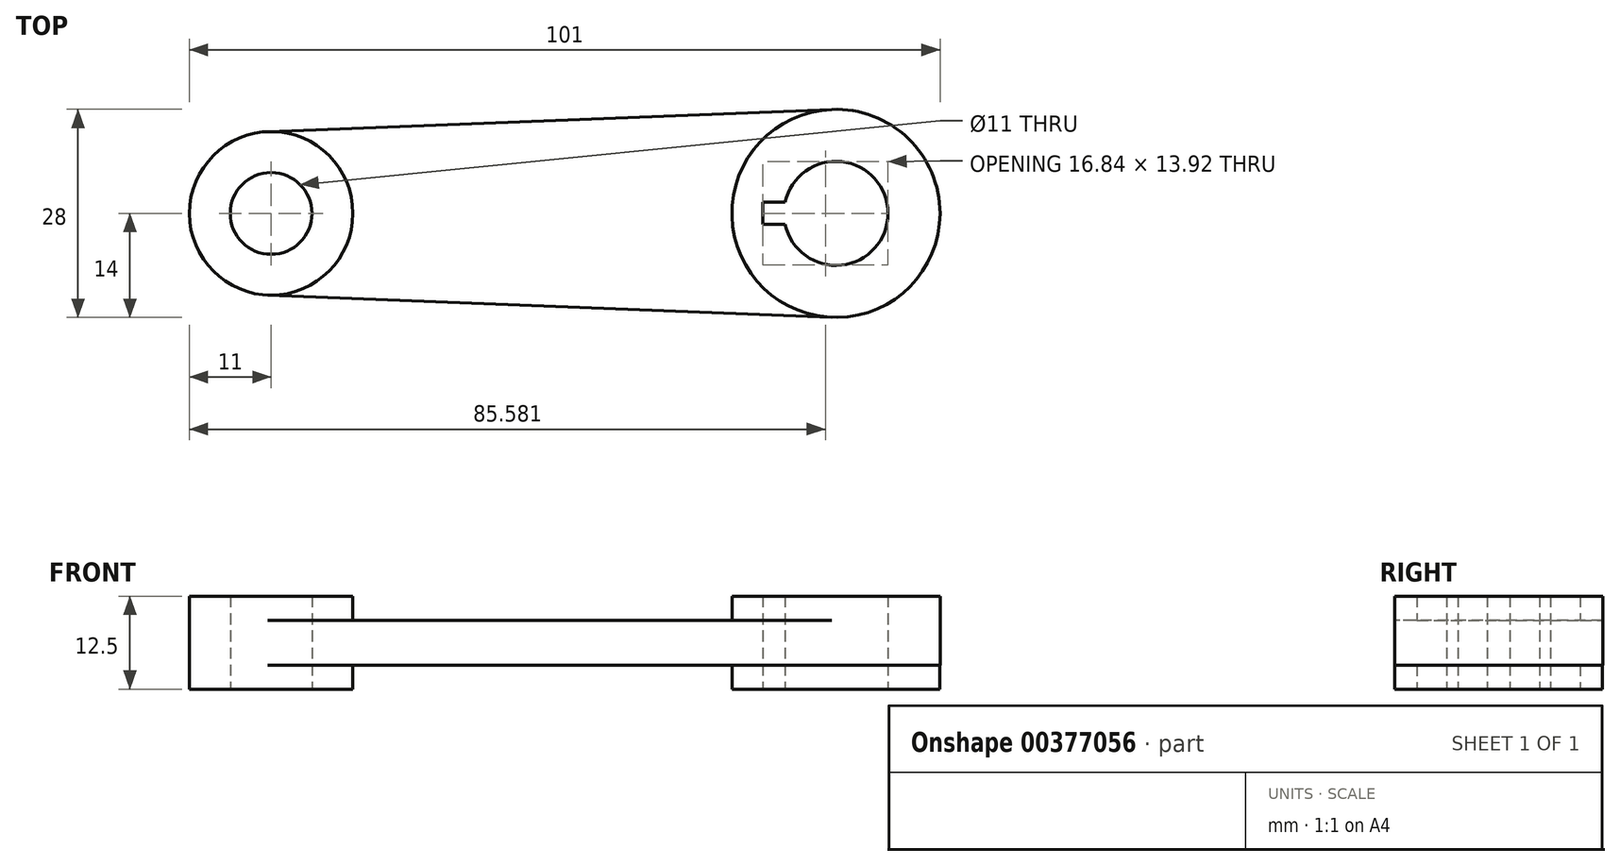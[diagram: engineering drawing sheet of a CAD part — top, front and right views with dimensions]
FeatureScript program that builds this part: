
annotation { "Feature Type Name" : "Feature", "Feature Type Description" : "" }
export const myFeature = defineFeature(function(context is Context, id is Id, definition is map)
    precondition{}
    {
        {
            var Q0;
            Q0=qCreatedBy(makeId("Top.planeOp"),FACE);
            var sketch = newSketch(context, id + "F0", { "sketchPlane" : qUnion([Q0])});
            skPoint(sketch, "E0", {"position": v(0, 0) * mm});
            skPoint(sketch, "E1", {"position": v(-38, 0) * mm});
            skPoint(sketch, "E2", {"position": v(38, 0) * mm});
            skArc(sketch, "E3", {"start": v(31.16, -1.5) * mm, "mid": v(45, 0) * mm, "end": v(31.16, 1.5) * mm});
            skCircle(sketch, "E4", {"center": v(38, 0) * mm, "radius": 14 * mm});
            skCircle(sketch, "E5", {"center": v(-38, 0) * mm, "radius": 5.5 * mm});
            skCircle(sketch, "E6", {"center": v(-38, 0) * mm, "radius": 11 * mm});
            skLineSegment(sketch, "E7", {"start": v(-38.43, 11) * mm, "end": v(37.45, 13.99) * mm});
            skLineSegment(sketch, "E8.MirrorCS", {"start": v(-38.43, -11) * mm, "end": v(37.45, -13.99) * mm});
            skLineSegment(sketch, "E9", {"start": v(28.16, 1.5) * mm, "end": v(31.16, 1.5) * mm});
            skLineSegment(sketch, "E10", {"start": v(28.16, -1.5) * mm, "end": v(31.16, -1.5) * mm});
            skLineSegment(sketch, "E11", {"start": v(28.16, 1.5) * mm, "end": v(28.16, -1.5) * mm});
            skPoint(sketch, "E12", {"position": v(28.16, 13.62) * mm});
            skPoint(sketch, "E13", {"position": v(28.16, -13.62) * mm});
            skArc(sketch, "E14", {"start": v(27.81, 13.6) * mm, "mid": v(21, 0) * mm, "end": v(27.81, -13.6) * mm});
            skPoint(sketch, "E15", {"position": v(21, 0) * mm});
            skPoint(sketch, "E16", {"position": v(24, 0) * mm});
            skPoint(sketch, "E17", {"position": v(-27, 0) * mm});
            skPoint(sketch, "E18", {"position": v(-24, 0) * mm});
            skArc(sketch, "E19", {"start": v(-29.78, -11.33) * mm, "mid": v(-24, 0) * mm, "end": v(-29.78, 11.33) * mm});
            skSolve(sketch);
        }
        {
            var Q0;
            {var subQ0=sQuery(id+"F0.wireOp",EDGE,"E14");Q0=makeQuery(id+"F0.imprint","IMPRINT",FACE,{"disambiguationData":[TD([[makeQuery(id+"F0.imprint","IMPRINT",EDGE,{"derivedFrom":subQ0}),-1.0]])]});}
            var Q1;
            {var subQ5=sQuery(id+"F0.wireOp",EDGE,"E19");Q1=makeQuery(id+"F0.imprint","IMPRINT",FACE,{"disambiguationData":[TD([[makeQuery(id+"F0.imprint","IMPRINT",EDGE,{"derivedFrom":subQ5}),1.0]])]});}
            var Q2;
            Q2=makeQuery(id+"F0.imprint","IMPRINT",FACE,{"disambiguationData":[TD([[makeQuery(id+"F0.imprint","IMPRINT",EDGE,{"derivedFrom":sQuery(id+"F0.wireOp",EDGE,"E5")}),-1.0]])]});
            var Q3;
            {var subQ5=sQuery(id+"F0.wireOp",EDGE,"E14");Q3=makeQuery(id+"F0.imprint","IMPRINT",FACE,{"disambiguationData":[TD([[makeQuery(id+"F0.imprint","IMPRINT",EDGE,{"derivedFrom":subQ5}),1.0]])]});}
            var Q4;
            Q4=makeQuery(id+"F0.imprint","IMPRINT",FACE,{"disambiguationData":[TD([[makeQuery(id+"F0.imprint","IMPRINT",EDGE,{"derivedFrom":sQuery(id+"F0.wireOp",EDGE,"E3")}),-1.0]])]});
            extrude(context, id + "F1", {"entities" : qUnion([Q0, Q1, Q2, Q3, Q4]), "depth" : 6 * mm});
        }
        {
            var Q0;
            Q0=makeQuery(id+"F1.opExtrude","CAP_FACE",FACE,{"disambiguationData":[OSD([sQuery(id+"F0.wireOp",EDGE,"E3"),sQuery(id+"F0.wireOp",EDGE,"E4"),sQuery(id+"F0.wireOp",EDGE,"E5"),sQuery(id+"F0.wireOp",EDGE,"E6"),sQuery(id+"F0.wireOp",EDGE,"E7"),sQuery(id+"F0.wireOp",EDGE,"E8.MirrorCS"),sQuery(id+"F0.wireOp",EDGE,"E9"),sQuery(id+"F0.wireOp",EDGE,"E10"),sQuery(id+"F0.wireOp",EDGE,"E11")])],"isStart":true});
            var sketch = newSketch(context, id + "F2", { "sketchPlane" : qUnion([Q0])});
            skPoint(sketch, "E20.0", {"position": v(0, 0) * mm});
            skPoint(sketch, "E20.1", {"position": v(-38, 0) * mm});
            skPoint(sketch, "E20.2", {"position": v(38, 0) * mm});
            skArc(sketch, "E20.3", {"start": v(31.16, 1.5) * mm, "mid": v(45, 0) * mm, "end": v(31.16, -1.5) * mm});
            skCircle(sketch, "E20.4", {"center": v(38, 0) * mm, "radius": 14 * mm});
            skCircle(sketch, "E20.5", {"center": v(-38, 0) * mm, "radius": 5.5 * mm});
            skCircle(sketch, "E20.6", {"center": v(-38, 0) * mm, "radius": 11 * mm});
            skLineSegment(sketch, "E20.7", {"start": v(-38.43, -11) * mm, "end": v(37.45, -13.99) * mm});
            skLineSegment(sketch, "E20.8", {"start": v(-38.43, 11) * mm, "end": v(37.45, 13.99) * mm});
            skLineSegment(sketch, "E20.9", {"start": v(28.16, -1.5) * mm, "end": v(31.16, -1.5) * mm});
            skLineSegment(sketch, "E20.10", {"start": v(28.16, 1.5) * mm, "end": v(31.16, 1.5) * mm});
            skLineSegment(sketch, "E20.11", {"start": v(28.16, -1.5) * mm, "end": v(28.16, 1.5) * mm});
            skPoint(sketch, "E20.12", {"position": v(28.16, -13.62) * mm});
            skPoint(sketch, "E20.13", {"position": v(28.16, 13.62) * mm});
            skArc(sketch, "E20.14", {"start": v(27.81, -13.6) * mm, "mid": v(21, 0) * mm, "end": v(27.81, 13.6) * mm});
            skPoint(sketch, "E20.15", {"position": v(21, 0) * mm});
            skPoint(sketch, "E20.16", {"position": v(24, 0) * mm});
            skPoint(sketch, "E20.17", {"position": v(-27, 0) * mm});
            skPoint(sketch, "E20.18", {"position": v(-24, 0) * mm});
            skArc(sketch, "E20.19", {"start": v(-29.78, 11.33) * mm, "mid": v(-24, 0) * mm, "end": v(-29.78, -11.33) * mm});
            skPoint(sketch, "E21", {"position": v(37.45, -13.99) * mm});
            skPoint(sketch, "E22", {"position": v(37.45, 13.99) * mm});
            skPoint(sketch, "E23", {"position": v(31.16, -1.5) * mm});
            skPoint(sketch, "E24", {"position": v(28.16, -1.5) * mm});
            skPoint(sketch, "E25", {"position": v(28.16, 1.5) * mm});
            skPoint(sketch, "E26", {"position": v(31.16, 1.5) * mm});
            skPoint(sketch, "E27", {"position": v(-29.78, -11.33) * mm});
            skPoint(sketch, "E28", {"position": v(-38.43, -11) * mm});
            skPoint(sketch, "E29", {"position": v(-38.43, 11) * mm});
            skPoint(sketch, "E30", {"position": v(-29.78, 11.33) * mm});
            skCircle(sketch, "E31", {"center": v(38, 0) * mm, "radius": 13.98 * mm});
            skSolve(sketch);
        }
        {
            var Q0;
            Q0=makeQuery(id+"F1.opExtrude","CAP_FACE",FACE,{"disambiguationData":[OSD([sQuery(id+"F0.wireOp",EDGE,"E3"),sQuery(id+"F0.wireOp",EDGE,"E4"),sQuery(id+"F0.wireOp",EDGE,"E5"),sQuery(id+"F0.wireOp",EDGE,"E6"),sQuery(id+"F0.wireOp",EDGE,"E7"),sQuery(id+"F0.wireOp",EDGE,"E8.MirrorCS"),sQuery(id+"F0.wireOp",EDGE,"E9"),sQuery(id+"F0.wireOp",EDGE,"E10"),sQuery(id+"F0.wireOp",EDGE,"E11")])],"isStart":false});
            var sketch = newSketch(context, id + "F3", { "sketchPlane" : qUnion([Q0])});
            skPoint(sketch, "E32", {"position": v(-29.78, 11.33) * mm});
            skPoint(sketch, "E33", {"position": v(-29.78, -11.33) * mm});
            skCircle(sketch, "E34", {"center": v(-38, 0) * mm, "radius": 11 * mm});
            skArc(sketch, "E35", {"start": v(-29.78, -11.33) * mm, "mid": v(-24, 0) * mm, "end": v(-29.78, 11.33) * mm});
            skCircle(sketch, "E36", {"center": v(38, 0) * mm, "radius": 14 * mm});
            skArc(sketch, "E37", {"start": v(27.81, 13.6) * mm, "mid": v(21, 0) * mm, "end": v(27.81, -13.6) * mm});
            skPoint(sketch, "E38", {"position": v(27.81, 13.6) * mm});
            skPoint(sketch, "E39", {"position": v(27.81, -13.6) * mm});
            skSolve(sketch);
        }
        {
            var Q0;
            Q0=makeQuery(id+"F3.imprint","IMPRINT",FACE,{"disambiguationData":[TD([[makeQuery(id+"F3.imprint","IMPRINT",EDGE,{"derivedFrom":makeQuery(id+"F1.opExtrude","CAP_EDGE",EDGE,{"disambiguationData":[OSD([sQuery(id+"F0.wireOp",EDGE,"E3")])],"isStart":false})}),-1.0]])]});
            extrude(context, id + "F4", {"entities" : qUnion([Q0]), "operationType" : NewBodyOperationType.ADD, "depth" : 3.25 * mm});
        }
        {
            var Q0;
            Q0=makeQuery(id+"F2.imprint","IMPRINT",FACE,{"disambiguationData":[TD([[makeQuery(id+"F2.imprint","IMPRINT",EDGE,{"derivedFrom":sQuery(id+"F2.wireOp",EDGE,"E20.3")}),1.0]])]});
            extrude(context, id + "F5", {"entities" : qUnion([Q0]), "operationType" : NewBodyOperationType.ADD, "depth" : 3.25 * mm});
        }
        {
            var Q0;
            Q0=makeQuery(id+"F3.imprint","IMPRINT",FACE,{"disambiguationData":[TD([[makeQuery(id+"F3.imprint","IMPRINT",EDGE,{"derivedFrom":makeQuery(id+"F1.opExtrude","CAP_EDGE",EDGE,{"disambiguationData":[OSD([sQuery(id+"F0.wireOp",EDGE,"E5")])],"isStart":false})}),-1.0]])]});
            extrude(context, id + "F6", {"entities" : qUnion([Q0]), "operationType" : NewBodyOperationType.ADD, "depth" : 3.25 * mm});
        }
        {
            var Q0;
            Q0=makeQuery(id+"F1.opExtrude","CAP_FACE",FACE,{"disambiguationData":[OSD([sQuery(id+"F0.wireOp",EDGE,"E3"),sQuery(id+"F0.wireOp",EDGE,"E4"),sQuery(id+"F0.wireOp",EDGE,"E5"),sQuery(id+"F0.wireOp",EDGE,"E6"),sQuery(id+"F0.wireOp",EDGE,"E7"),sQuery(id+"F0.wireOp",EDGE,"E8.MirrorCS"),sQuery(id+"F0.wireOp",EDGE,"E9"),sQuery(id+"F0.wireOp",EDGE,"E10"),sQuery(id+"F0.wireOp",EDGE,"E11")])],"isStart":true});
            var sketch = newSketch(context, id + "F7", { "sketchPlane" : qUnion([Q0])});
            skPoint(sketch, "E40.0", {"position": v(-29.78, -11.33) * mm});
            skPoint(sketch, "E40.1", {"position": v(-29.78, 11.33) * mm});
            skCircle(sketch, "E40.2", {"center": v(-38, 0) * mm, "radius": 11 * mm});
            skArc(sketch, "E40.3", {"start": v(-29.78, 11.33) * mm, "mid": v(-24, 0) * mm, "end": v(-29.78, -11.33) * mm});
            skCircle(sketch, "E40.4", {"center": v(38, 0) * mm, "radius": 14 * mm});
            skArc(sketch, "E40.5", {"start": v(27.81, -13.6) * mm, "mid": v(21, 0) * mm, "end": v(27.81, 13.6) * mm});
            skPoint(sketch, "E40.6", {"position": v(27.81, -13.6) * mm});
            skPoint(sketch, "E40.7", {"position": v(27.81, 13.6) * mm});
            skSolve(sketch);
        }
        {
            var Q0;
            Q0=makeQuery(id+"F7.imprint","IMPRINT",FACE,{"disambiguationData":[TD([[makeQuery(id+"F7.imprint","IMPRINT",EDGE,{"derivedFrom":makeQuery(id+"F1.opExtrude","CAP_EDGE",EDGE,{"disambiguationData":[OSD([sQuery(id+"F0.wireOp",EDGE,"E5")])],"isStart":true})}),1.0]])]});
            extrude(context, id + "F8", {"entities" : qUnion([Q0]), "operationType" : NewBodyOperationType.ADD, "depth" : 3.25 * mm});
        }
    });
